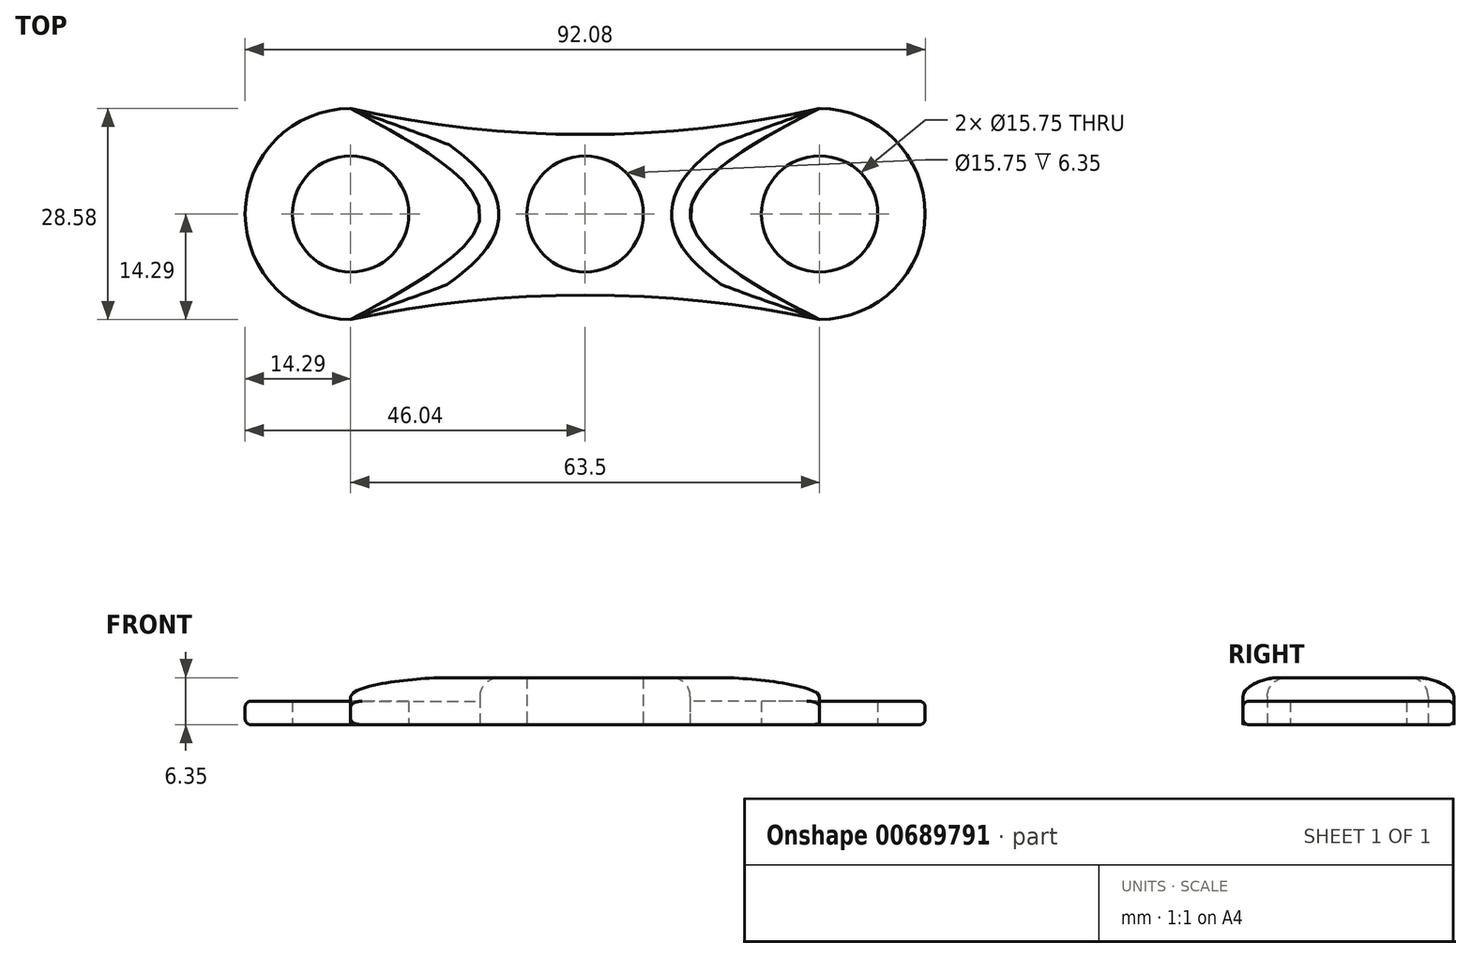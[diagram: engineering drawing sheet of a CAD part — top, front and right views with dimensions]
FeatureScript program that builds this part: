
annotation { "Feature Type Name" : "Feature", "Feature Type Description" : "" }
export const myFeature = defineFeature(function(context is Context, id is Id, definition is map)
    precondition{}
    {
        {
            var Q0;
            Q0=qCreatedBy(makeId("Top.planeOp"),FACE);
            var sketch = newSketch(context, id + "F0", { "sketchPlane" : qUnion([Q0])});
            skPoint(sketch, "E0.middle", {"position": v(3.14, 0) * mm});
            skArc(sketch, "E1", {"start": v(34.9, -14.29) * mm, "mid": v(49.18, 0) * mm, "end": v(34.9, 14.29) * mm});
            skArc(sketch, "E2", {"start": v(-28.6, 14.29) * mm, "mid": v(-42.9, 0) * mm, "end": v(-28.6, -14.29) * mm});
            skCircle(sketch, "E3", {"center": v(-28.6, 0) * mm, "radius": 7.87 * mm});
            skCircle(sketch, "E4", {"center": v(34.9, 0) * mm, "radius": 7.87 * mm});
            skArc(sketch, "E5", {"start": v(-28.6, 14.29) * mm, "mid": v(3.14, 10.76) * mm, "end": v(34.9, 14.29) * mm});
            skArc(sketch, "E6", {"start": v(34.9, -14.29) * mm, "mid": v(3.14, -11) * mm, "end": v(-28.6, -14.29) * mm});
            skCircle(sketch, "E7", {"center": v(3.14, 0) * mm, "radius": 7.87 * mm});
            skFitSpline(sketch, "E8", {"points": [v(-28.6, 14.29) * mm, v(-11.08, 0) * mm, v(-28.6, -14.29) * mm], "startDerivative": vector(52.6, -28.58) * mm, "endDerivative": vector(-52.6, -28.58) * mm});
            skFitSpline(sketch, "E9", {"points": [v(34.9, 14.29) * mm, v(17.36, 0) * mm, v(34.9, -14.29) * mm], "startDerivative": vector(-57.24, -28.58) * mm, "endDerivative": vector(57.24, -28.57) * mm});
            skSolve(sketch);
        }
        {
            var Q0;
            Q0=makeQuery(id+"F0.imprint","IMPRINT",FACE,{"disambiguationData":[TD([[makeQuery(id+"F0.imprint","IMPRINT",EDGE,{"derivedFrom":sQuery(id+"F0.wireOp",EDGE,"E2")}),1.0]])]});
            var Q1;
            Q1=makeQuery(id+"F0.imprint","IMPRINT",FACE,{"disambiguationData":[TD([[makeQuery(id+"F0.imprint","IMPRINT",EDGE,{"derivedFrom":sQuery(id+"F0.wireOp",EDGE,"E1")}),1.0]])]});
            extrude(context, id + "F1", {"entities" : qUnion([Q0, Q1]), "depth" : 3.17 * mm, "offsetDistance" : 25.4 * mm});
        }
        {
            var Q0;
            Q0=makeQuery(id+"F0.imprint","IMPRINT",FACE,{"disambiguationData":[TD([[makeQuery(id+"F0.imprint","IMPRINT",EDGE,{"derivedFrom":sQuery(id+"F0.wireOp",EDGE,"E5")}),-1.0]])]});
            extrude(context, id + "F2", {"entities" : qUnion([Q0]), "depth" : 6.35 * mm, "offsetDistance" : 25.4 * mm});
        }
        {
            var Q0;
            Q0=makeQuery(id+"F1.opExtrude","CAP_EDGE",EDGE,{"disambiguationData":[OSD([sQuery(id+"F0.wireOp",EDGE,"E2")])],"isStart":false});
            var Q1;
            Q1=makeQuery(id+"F1.opExtrude","CAP_EDGE",EDGE,{"disambiguationData":[OSD([sQuery(id+"F0.wireOp",EDGE,"E1")])],"isStart":false});
            var Q2;
            Q2=makeQuery(id+"F1.opExtrude","CAP_EDGE",EDGE,{"disambiguationData":[OSD([sQuery(id+"F0.wireOp",EDGE,"E1")])],"isStart":true});
            var Q3;
            Q3=makeQuery(id+"F1.opExtrude","CAP_EDGE",EDGE,{"disambiguationData":[OSD([sQuery(id+"F0.wireOp",EDGE,"E2")])],"isStart":true});
            fillet(context, id + "F3", {"entities" : qUnion([Q0, Q1, Q2, Q3]), "radius" : 0.76 * mm, "tangentPropagation" : true, "allowEdgeOverflow" : false});
        }
        {
            var Q0;
            Q0=makeQuery(id+"F2.opExtrude","CAP_EDGE",EDGE,{"disambiguationData":[OSD([sQuery(id+"F0.wireOp",EDGE,"E6")])],"isStart":false});
            var Q1;
            Q1=makeQuery(id+"F2.opExtrude","CAP_EDGE",EDGE,{"disambiguationData":[OSD([sQuery(id+"F0.wireOp",EDGE,"E5")])],"isStart":false});
            var Q2;
            Q2=makeQuery(id+"F2.opExtrude","CAP_EDGE",EDGE,{"disambiguationData":[OSD([sQuery(id+"F0.wireOp",EDGE,"E9")])],"isStart":false});
            var Q3;
            Q3=makeQuery(id+"F2.opExtrude","CAP_EDGE",EDGE,{"disambiguationData":[OSD([sQuery(id+"F0.wireOp",EDGE,"E8")])],"isStart":false});
            fillet(context, id + "F4", {"entities" : qUnion([Q0, Q1, Q2, Q3]), "radius" : 2.54 * mm, "tangentPropagation" : true, "allowEdgeOverflow" : false});
        }
    });
